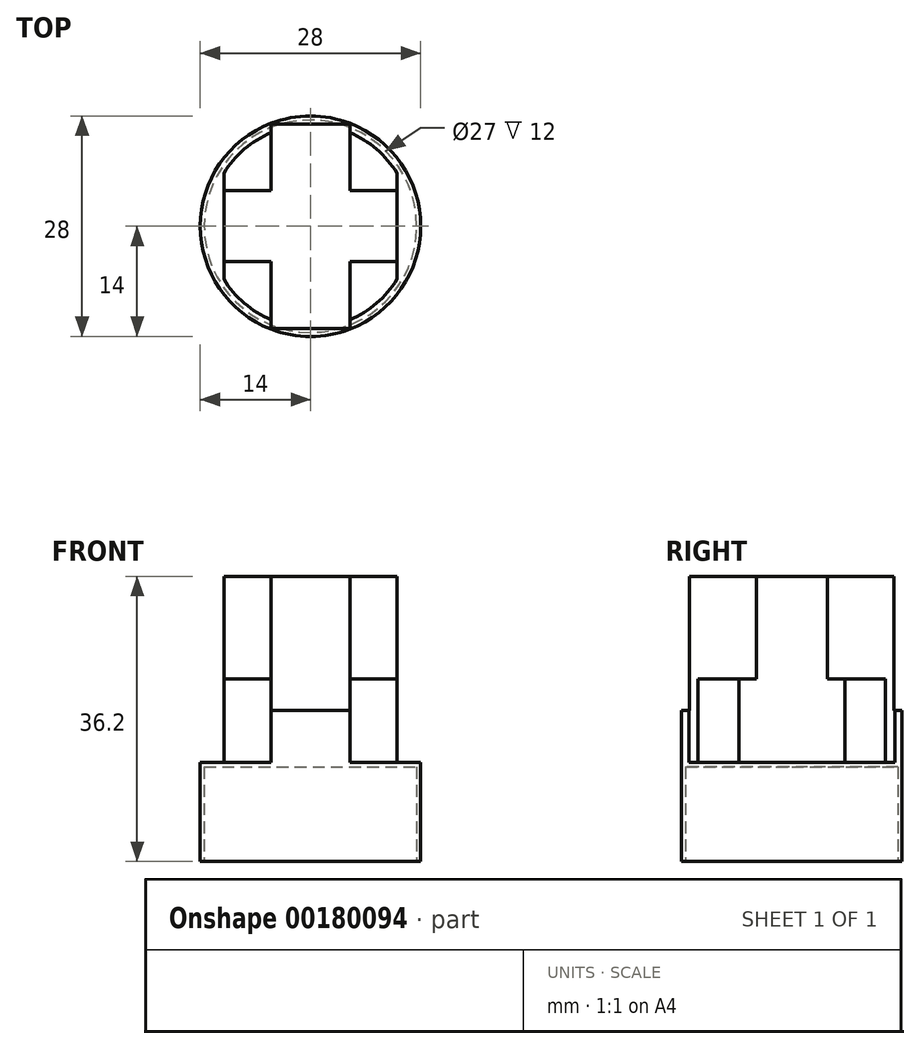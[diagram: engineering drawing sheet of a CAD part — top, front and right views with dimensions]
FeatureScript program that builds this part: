
annotation { "Feature Type Name" : "Feature", "Feature Type Description" : "" }
export const myFeature = defineFeature(function(context is Context, id is Id, definition is map)
    precondition{}
    {
        {
            var Q0;
            Q0=qCreatedBy(makeId("Top.planeOp"),FACE);
            var sketch = newSketch(context, id + "F0", { "sketchPlane" : qUnion([Q0])});
            skCircle(sketch, "E0", {"center": v(0, 0) * mm, "radius": 14 * mm});
            skSolve(sketch);
        }
        {
            var Q0;
            Q0 = qSketchRegion(id + "F0", true);
            extrude(context, id + "F1", {"entities" : qUnion([Q0]), "depth" : 12.6 * mm});
        }
        {
            var Q0;
            Q0=makeQuery(id+"F1.opExtrude","CAP_FACE",FACE,{"disambiguationData":[OSD([sQuery(id+"F0.wireOp",EDGE,"E0")])],"isStart":false});
            var sketch = newSketch(context, id + "F2", { "sketchPlane" : qUnion([Q0])});
            skCircle(sketch, "E1", {"center": v(0, 0) * mm, "radius": 12.9 * mm});
            skSolve(sketch);
        }
        {
            var Q0;
            Q0 = qSketchRegion(id + "F2", true);
            extrude(context, id + "F3", {"entities" : qUnion([Q0]), "operationType" : NewBodyOperationType.ADD, "depth" : 10.6 * mm});
        }
        {
            var Q0;
            Q0=makeQuery(id+"F3.opExtrude","CAP_FACE",FACE,{"disambiguationData":[OSD([sQuery(id+"F2.wireOp",EDGE,"E1")])],"isStart":false});
            var sketch = newSketch(context, id + "F4", { "sketchPlane" : qUnion([Q0])});
            skLineSegment(sketch, "E2.bottom", {"start": v(11, 38.1) * mm, "end": v(-11, 38.1) * mm});
            skLineSegment(sketch, "E2.top", {"start": v(11, -38.1) * mm, "end": v(-11, -38.1) * mm});
            skLineSegment(sketch, "E2.left", {"start": v(11, 38.1) * mm, "end": v(11, -38.1) * mm});
            skLineSegment(sketch, "E2.right", {"start": v(-11, 38.1) * mm, "end": v(-11, -38.1) * mm});
            skPoint(sketch, "E2.middle", {"position": v(0, 0) * mm});
            skLineSegment(sketch, "E3.bottom", {"start": v(-20.84, 13.91) * mm, "end": v(-1.16, 13.91) * mm});
            skLineSegment(sketch, "E3.top", {"start": v(-20.84, -13.91) * mm, "end": v(-1.16, -13.91) * mm});
            skLineSegment(sketch, "E3.left", {"start": v(-20.84, 13.91) * mm, "end": v(-20.84, -13.91) * mm});
            skLineSegment(sketch, "E3.right", {"start": v(-1.16, 13.91) * mm, "end": v(-1.16, -13.91) * mm});
            skPoint(sketch, "E3.middle", {"position": v(-11, 0) * mm});
            skLineSegment(sketch, "E4.bottom", {"start": v(19.01, 15.17) * mm, "end": v(2.99, 15.17) * mm});
            skLineSegment(sketch, "E4.top", {"start": v(19.01, -15.17) * mm, "end": v(2.99, -15.17) * mm});
            skLineSegment(sketch, "E4.left", {"start": v(19.01, 15.17) * mm, "end": v(19.01, -15.17) * mm});
            skLineSegment(sketch, "E4.right", {"start": v(2.99, 15.17) * mm, "end": v(2.99, -15.17) * mm});
            skPoint(sketch, "E4.middle", {"position": v(11, 0) * mm});
            skSolve(sketch);
        }
        {
            var Q0;
            {var subQ0=sQuery(id+"F4.wireOp",EDGE,"E4.left");Q0=makeQuery(id+"F4.imprint","IMPRINT",FACE,{"disambiguationData":[TD([[makeQuery(id+"F4.imprint","IMPRINT",EDGE,{"derivedFrom":subQ0}),-1.0]])]});}
            var Q1;
            {var subQ0=sQuery(id+"F4.wireOp",EDGE,"E2.right");var subQ1=makeQuery(id+"F3.opExtrude","CAP_EDGE",EDGE,{"disambiguationData":[OSD([sQuery(id+"F2.wireOp",EDGE,"E1")])],"isStart":false});var subQ2=makeQuery(id+"F4.imprint","INTERSECT",VERTEX,{"disambiguationData":[OD(0.0)],"derivedFrom":[subQ1,subQ0]});Q1=makeQuery(id+"F4.imprint","IMPRINT",FACE,{"disambiguationData":[TD([[makeQuery(id+"F4.imprint","IMPRINT",EDGE,{"disambiguationData":[TD([[subQ2,-1.0]])],"derivedFrom":subQ0}),-1.0]])]});}
            var Q2;
            {var subQ0=sQuery(id+"F4.wireOp",EDGE,"E3.left");Q2=makeQuery(id+"F4.imprint","IMPRINT",FACE,{"disambiguationData":[TD([[makeQuery(id+"F4.imprint","IMPRINT",EDGE,{"derivedFrom":subQ0}),1.0]])]});}
            var Q3;
            {var subQ0=sQuery(id+"F4.wireOp",EDGE,"E2.left");var subQ1=makeQuery(id+"F3.opExtrude","CAP_EDGE",EDGE,{"disambiguationData":[OSD([sQuery(id+"F2.wireOp",EDGE,"E1")])],"isStart":false});var subQ2=makeQuery(id+"F4.imprint","INTERSECT",VERTEX,{"disambiguationData":[OD(0.0)],"derivedFrom":[subQ1,subQ0]});Q3=makeQuery(id+"F4.imprint","IMPRINT",FACE,{"disambiguationData":[TD([[makeQuery(id+"F4.imprint","IMPRINT",EDGE,{"disambiguationData":[TD([[subQ2,-1.0]])],"derivedFrom":subQ0}),1.0]])]});}
            extrude(context, id + "F5", {"entities" : qUnion([Q0, Q1, Q2, Q3]), "operationType" : NewBodyOperationType.REMOVE, "oppositeDirection" : true, "depth" : 10.6 * mm});
        }
        {
            var Q0;
            Q0=makeQuery(id+"F3.opExtrude","CAP_FACE",FACE,{"disambiguationData":[OSD([sQuery(id+"F2.wireOp",EDGE,"E1")])],"isStart":false});
            var sketch = newSketch(context, id + "F6", { "sketchPlane" : qUnion([Q0])});
            skLineSegment(sketch, "E5.bottom", {"start": v(-11, 4.5) * mm, "end": v(11, 4.5) * mm});
            skLineSegment(sketch, "E5.top", {"start": v(-11, -4.5) * mm, "end": v(11, -4.5) * mm});
            skLineSegment(sketch, "E5.left", {"start": v(-11, 4.5) * mm, "end": v(-11, -4.5) * mm});
            skLineSegment(sketch, "E5.right", {"start": v(11, 4.5) * mm, "end": v(11, -4.5) * mm});
            skPoint(sketch, "E5.middle", {"position": v(0, 0) * mm});
            skLineSegment(sketch, "E6.bottom", {"start": v(5, -13) * mm, "end": v(-5, -13) * mm});
            skLineSegment(sketch, "E6.top", {"start": v(5, 13) * mm, "end": v(-5, 13) * mm});
            skLineSegment(sketch, "E6.left", {"start": v(5, -13) * mm, "end": v(5, 13) * mm});
            skLineSegment(sketch, "E6.right", {"start": v(-5, -13) * mm, "end": v(-5, 13) * mm});
            skSolve(sketch);
        }
        {
            var Q0;
            Q0 = qSketchRegion(id + "F6", true);
            extrude(context, id + "F7", {"entities" : qUnion([Q0]), "operationType" : NewBodyOperationType.ADD, "depth" : 13 * mm, "hasSecondDirection" : true, "secondDirectionOppositeDirection" : true, "secondDirectionDepth" : 12 * mm});
        }
        {
            var Q0;
            Q0=makeQuery(id+"F5.boolean.opBoolean","MERGE",FACE,{"derivedFrom":[makeQuery(id+"F1.opExtrude","CAP_FACE",FACE,{"disambiguationData":[OSD([sQuery(id+"F0.wireOp",EDGE,"E0")])],"isStart":false}),makeQuery(id+"F5.opExtrude","CAP_FACE",FACE,{"disambiguationData":[OSD([sQuery(id+"F4.wireOp",EDGE,"E2.left"),sQuery(id+"F4.wireOp",EDGE,"E4.bottom"),sQuery(id+"F4.wireOp",EDGE,"E4.top"),sQuery(id+"F4.wireOp",EDGE,"E4.left")])],"isStart":false}),makeQuery(id+"F5.opExtrude","CAP_FACE",FACE,{"disambiguationData":[OSD([sQuery(id+"F4.wireOp",EDGE,"E2.right"),sQuery(id+"F4.wireOp",EDGE,"E3.bottom"),sQuery(id+"F4.wireOp",EDGE,"E3.top"),sQuery(id+"F4.wireOp",EDGE,"E3.left")])],"isStart":false})]});
            var sketch = newSketch(context, id + "F8", { "sketchPlane" : qUnion([Q0])});
            skLineSegment(sketch, "E7.0", {"start": v(-5, -13) * mm, "end": v(5, -13) * mm});
            skCircle(sketch, "E8.0", {"center": v(0, 0) * mm, "radius": 14 * mm});
            skLineSegment(sketch, "E9.0", {"start": v(-5, 13) * mm, "end": v(5, 13) * mm});
            skLineSegment(sketch, "E10", {"start": v(5, 13) * mm, "end": v(5, 14.16) * mm});
            skLineSegment(sketch, "E11", {"start": v(-5, 13) * mm, "end": v(-5, 14.17) * mm});
            skLineSegment(sketch, "E12", {"start": v(-5, -13) * mm, "end": v(-5, -13.66) * mm});
            skLineSegment(sketch, "E13", {"start": v(5, -13) * mm, "end": v(5, -13.7) * mm});
            skSolve(sketch);
        }
        {
            var Q0;
            {var subQ0=sQuery(id+"F8.wireOp",EDGE,"E7.0");Q0=makeQuery(id+"F8.imprint","IMPRINT",FACE,{"disambiguationData":[TD([[makeQuery(id+"F8.imprint","IMPRINT",EDGE,{"derivedFrom":subQ0}),-1.0]])]});}
            var Q1;
            {var subQ5=sQuery(id+"F8.wireOp",EDGE,"E9.0");Q1=makeQuery(id+"F8.imprint","IMPRINT",FACE,{"disambiguationData":[TD([[makeQuery(id+"F8.imprint","IMPRINT",EDGE,{"derivedFrom":subQ5}),1.0]])]});}
            extrude(context, id + "F9", {"entities" : qUnion([Q0, Q1]), "operationType" : NewBodyOperationType.ADD, "depth" : 6.6 * mm});
        }
        {
            var Q0;
            Q0=makeQuery(id+"F1.opExtrude","CAP_FACE",FACE,{"disambiguationData":[OSD([sQuery(id+"F0.wireOp",EDGE,"E0")])],"isStart":true});
            var sketch = newSketch(context, id + "F10", { "sketchPlane" : qUnion([Q0])});
            skCircle(sketch, "E14", {"center": v(0, 0) * mm, "radius": 13.5 * mm});
            skSolve(sketch);
        }
        {
            var Q0;
            Q0 = qSketchRegion(id + "F10", true);
            extrude(context, id + "F11", {"entities" : qUnion([Q0]), "operationType" : NewBodyOperationType.REMOVE, "oppositeDirection" : true, "depth" : 12 * mm});
        }
    });
